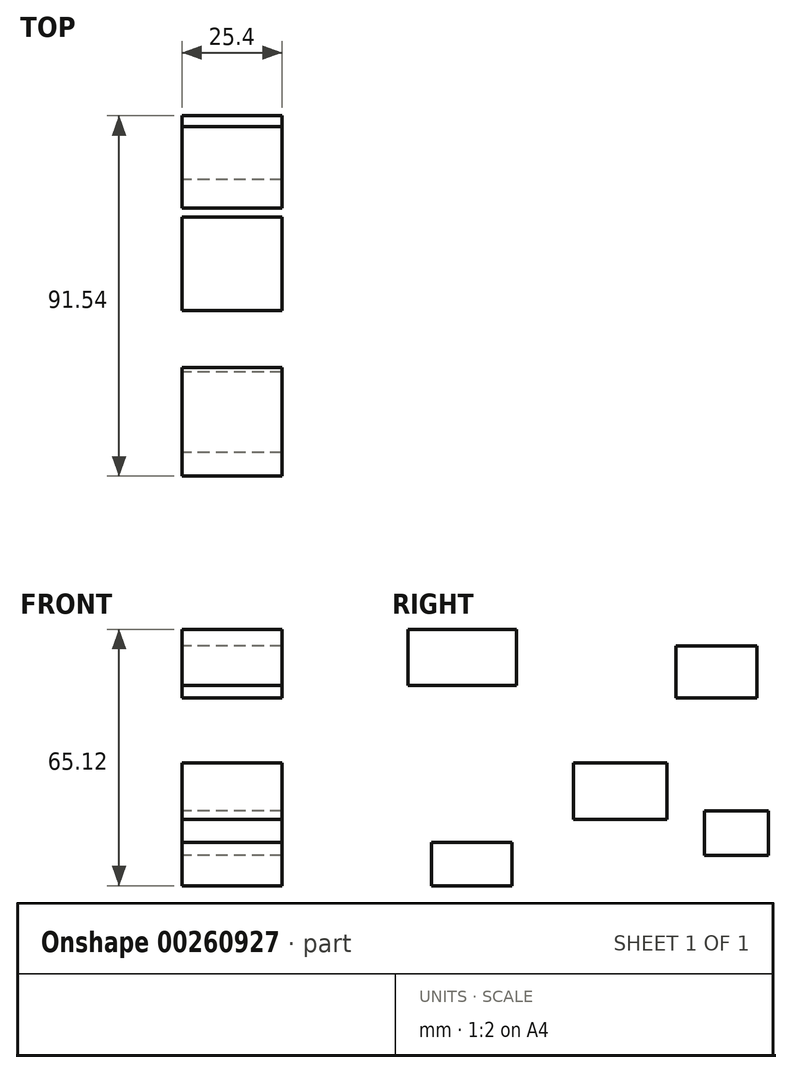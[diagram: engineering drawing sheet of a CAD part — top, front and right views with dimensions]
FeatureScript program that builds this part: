
annotation { "Feature Type Name" : "Feature", "Feature Type Description" : "" }
export const myFeature = defineFeature(function(context is Context, id is Id, definition is map)
    precondition{}
    {
        {
            var Q0;
            Q0=qCreatedBy(makeId("Right.planeOp"),FACE);
            var sketch = newSketch(context, id + "F0", { "sketchPlane" : qUnion([Q0])});
            skLineSegment(sketch, "E0.bottom", {"start": v(-42.1, 39.7) * mm, "end": v(-14.52, 39.7) * mm});
            skLineSegment(sketch, "E0.top", {"start": v(-42.1, 25.49) * mm, "end": v(-14.52, 25.49) * mm});
            skLineSegment(sketch, "E0.left", {"start": v(-42.1, 39.7) * mm, "end": v(-42.1, 25.49) * mm});
            skLineSegment(sketch, "E0.right", {"start": v(-14.52, 39.7) * mm, "end": v(-14.52, 25.49) * mm});
            skSolve(sketch);
        }
        {
            var Q0;
            Q0=makeQuery(id+"F0.imprint","IMPRINT",FACE,{"disambiguationData":[TD([[makeQuery(id+"F0.imprint","IMPRINT",EDGE,{"derivedFrom":sQuery(id+"F0.wireOp",EDGE,"E0.bottom")}),-1.0]])]});
            extrude(context, id + "F1", {"entities" : qUnion([Q0]), "depth" : 25.4 * mm});
        }
        {
            var Q0;
            Q0=qCreatedBy(makeId("Right.planeOp"),FACE);
            var sketch = newSketch(context, id + "F2", { "sketchPlane" : qUnion([Q0])});
            skLineSegment(sketch, "E1.bottom", {"start": v(46.62, 35.5) * mm, "end": v(26, 35.5) * mm});
            skLineSegment(sketch, "E1.top", {"start": v(46.62, 22.37) * mm, "end": v(26, 22.37) * mm});
            skLineSegment(sketch, "E1.left", {"start": v(46.62, 35.5) * mm, "end": v(46.62, 22.37) * mm});
            skLineSegment(sketch, "E1.right", {"start": v(26, 35.5) * mm, "end": v(26, 22.37) * mm});
            skSolve(sketch);
        }
        {
            var Q0;
            Q0=qCreatedBy(makeId("Right.planeOp"),FACE);
            var sketch = newSketch(context, id + "F3", { "sketchPlane" : qUnion([Q0])});
            skLineSegment(sketch, "E2.bottom", {"start": v(49.44, -6.44) * mm, "end": v(33.27, -6.44) * mm});
            skLineSegment(sketch, "E2.top", {"start": v(49.44, -17.69) * mm, "end": v(33.27, -17.69) * mm});
            skLineSegment(sketch, "E2.left", {"start": v(49.44, -6.44) * mm, "end": v(49.44, -17.69) * mm});
            skLineSegment(sketch, "E2.right", {"start": v(33.27, -6.44) * mm, "end": v(33.27, -17.69) * mm});
            skSolve(sketch);
        }
        {
            var Q0;
            Q0=qCreatedBy(makeId("Right.planeOp"),FACE);
            var sketch = newSketch(context, id + "F4", { "sketchPlane" : qUnion([Q0])});
            skLineSegment(sketch, "E3.bottom", {"start": v(-15.7, -14.4) * mm, "end": v(-36.08, -14.4) * mm});
            skLineSegment(sketch, "E3.top", {"start": v(-15.7, -25.42) * mm, "end": v(-36.08, -25.42) * mm});
            skLineSegment(sketch, "E3.left", {"start": v(-15.7, -14.4) * mm, "end": v(-15.7, -25.42) * mm});
            skLineSegment(sketch, "E3.right", {"start": v(-36.08, -14.4) * mm, "end": v(-36.08, -25.42) * mm});
            skSolve(sketch);
        }
        {
            var Q0;
            Q0=qCreatedBy(makeId("Right.planeOp"),FACE);
            var sketch = newSketch(context, id + "F5", { "sketchPlane" : qUnion([Q0])});
            skLineSegment(sketch, "E4.bottom", {"start": v(23.66, 5.74) * mm, "end": v(0, 5.74) * mm});
            skLineSegment(sketch, "E4.top", {"start": v(23.66, -8.55) * mm, "end": v(0, -8.55) * mm});
            skLineSegment(sketch, "E4.left", {"start": v(23.66, 5.74) * mm, "end": v(23.66, -8.55) * mm});
            skLineSegment(sketch, "E4.right", {"start": v(0, 5.74) * mm, "end": v(0, -8.55) * mm});
            skSolve(sketch);
        }
        {
            var Q0;
            Q0=makeQuery(id+"F2.imprint","IMPRINT",FACE,{"disambiguationData":[TD([[makeQuery(id+"F2.imprint","IMPRINT",EDGE,{"derivedFrom":sQuery(id+"F2.wireOp",EDGE,"E1.bottom")}),1.0]])]});
            extrude(context, id + "F6", {"entities" : qUnion([Q0]), "depth" : 25.4 * mm});
        }
        {
            var Q0;
            Q0=makeQuery(id+"F3.imprint","IMPRINT",FACE,{"disambiguationData":[TD([[makeQuery(id+"F3.imprint","IMPRINT",EDGE,{"derivedFrom":sQuery(id+"F3.wireOp",EDGE,"E2.bottom")}),1.0]])]});
            extrude(context, id + "F7", {"entities" : qUnion([Q0]), "depth" : 25.4 * mm});
        }
        {
            var Q0;
            Q0=makeQuery(id+"F5.imprint","IMPRINT",FACE,{"disambiguationData":[TD([[makeQuery(id+"F5.imprint","IMPRINT",EDGE,{"derivedFrom":sQuery(id+"F5.wireOp",EDGE,"E4.bottom")}),1.0]])]});
            extrude(context, id + "F8", {"entities" : qUnion([Q0]), "depth" : 25.4 * mm});
        }
        {
            var Q0;
            Q0=makeQuery(id+"F4.imprint","IMPRINT",FACE,{"disambiguationData":[TD([[makeQuery(id+"F4.imprint","IMPRINT",EDGE,{"derivedFrom":sQuery(id+"F4.wireOp",EDGE,"E3.bottom")}),1.0]])]});
            extrude(context, id + "F9", {"entities" : qUnion([Q0]), "depth" : 25.4 * mm});
        }
    });
